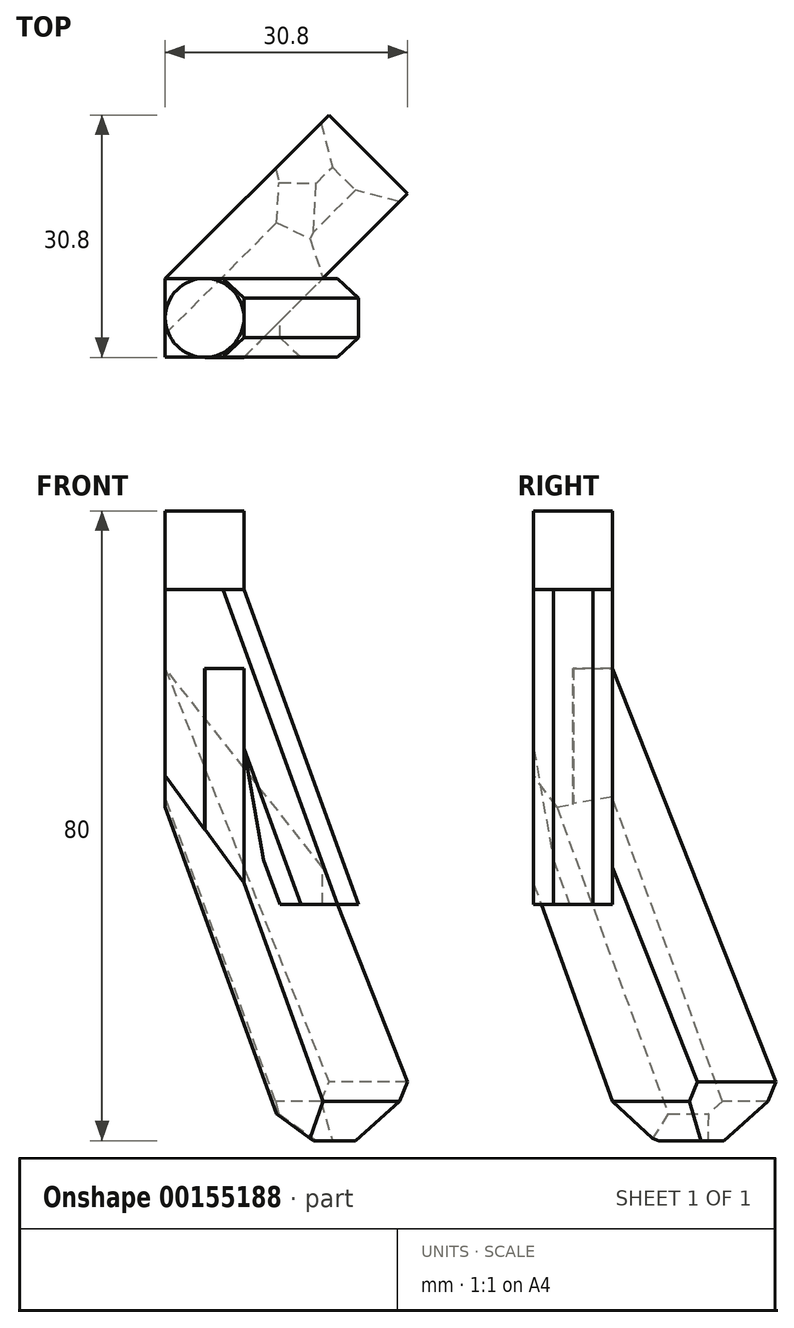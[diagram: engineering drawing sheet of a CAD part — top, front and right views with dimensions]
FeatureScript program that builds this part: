
annotation { "Feature Type Name" : "Feature", "Feature Type Description" : "" }
export const myFeature = defineFeature(function(context is Context, id is Id, definition is map)
    precondition{}
    {
        {
            var Q0;
            Q0=qCreatedBy(makeId("Top.planeOp"),FACE);
            var sketch = newSketch(context, id + "F0", { "sketchPlane" : qUnion([Q0])});
            skCircle(sketch, "E0", {"center": v(0, 0) * mm, "radius": 5 * mm});
            skSolve(sketch);
        }
        {
            var Q0;
            Q0=qSketchRegion(id+"F0",true);
            extrude(context, id + "F1", {"entities" : qUnion([Q0]), "oppositeDirection" : true, "depth" : 10 * mm});
        }
        {
            var Q0;
            Q0=makeQuery(id+"F1.opExtrude","CAP_FACE",FACE,{"disambiguationData":[OSD([sQuery(id+"F0.wireOp",EDGE,"E0")])],"isStart":false});
            var sketch = newSketch(context, id + "F2", { "sketchPlane" : qUnion([Q0])});
            skLineSegment(sketch, "E1.bottom", {"start": v(5, -5) * mm, "end": v(-5, -5) * mm});
            skLineSegment(sketch, "E1.top", {"start": v(5, 5) * mm, "end": v(-5, 5) * mm});
            skLineSegment(sketch, "E1.left", {"start": v(5, -5) * mm, "end": v(5, 5) * mm});
            skLineSegment(sketch, "E1.right", {"start": v(-5, -5) * mm, "end": v(-5, 5) * mm});
            skPoint(sketch, "E1.middle", {"position": v(0, 0) * mm});
            skSolve(sketch);
        }
        {
            var Q0;
            Q0=qSketchRegion(id+"F2",true);
            extrude(context, id + "F3", {"entities" : qUnion([Q0]), "operationType" : NewBodyOperationType.ADD, "depth" : 10 * mm});
        }
        {
            var Q0;
            Q0=makeQuery(id+"F3.opExtrude","CAP_FACE",FACE,{"disambiguationData":[OSD([sQuery(id+"F2.wireOp",EDGE,"E1.bottom"),sQuery(id+"F2.wireOp",EDGE,"E1.top"),sQuery(id+"F2.wireOp",EDGE,"E1.left"),sQuery(id+"F2.wireOp",EDGE,"E1.right")])],"isStart":false});
            var sketch = newSketch(context, id + "F4", { "sketchPlane" : qUnion([Q0])});
            skLineSegment(sketch, "E2", {"start": v(0, 5) * mm, "end": v(-5, 0) * mm});
            skLineSegment(sketch, "E3", {"start": v(-5, 0) * mm, "end": v(0, -5) * mm});
            skLineSegment(sketch, "E4", {"start": v(0, -5) * mm, "end": v(5, 0) * mm});
            skLineSegment(sketch, "E5", {"start": v(5, 0) * mm, "end": v(0, 5) * mm});
            skLineSegment(sketch, "E6", {"start": v(0, -5) * mm, "end": v(-2.5, -7.5) * mm});
            skLineSegment(sketch, "E7", {"start": v(-2.5, -7.5) * mm, "end": v(-5, -5) * mm});
            skLineSegment(sketch, "E8", {"start": v(-5, -5) * mm, "end": v(-7.5, -2.5) * mm});
            skLineSegment(sketch, "E9", {"start": v(-7.5, -2.5) * mm, "end": v(-5, 0) * mm});
            skLineSegment(sketch, "E10", {"start": v(0, 0) * mm, "end": v(5, -5) * mm});
            skLineSegment(sketch, "E11", {"start": v(5, -5) * mm, "end": v(-5, 5) * mm});
            skLineSegment(sketch, "E12.MirrorCS", {"start": v(5, 0) * mm, "end": v(7.5, 2.5) * mm});
            skLineSegment(sketch, "E13.MirrorCS", {"start": v(7.5, 2.5) * mm, "end": v(5, 5) * mm});
            skLineSegment(sketch, "E14.MirrorCS", {"start": v(5, 5) * mm, "end": v(2.5, 7.5) * mm});
            skLineSegment(sketch, "E15.MirrorCS", {"start": v(2.5, 7.5) * mm, "end": v(0, 5) * mm});
            skSolve(sketch);
        }
        {
            var Q0;
            {var subQ0=sQuery(id+"F4.wireOp",EDGE,"E6");Q0=makeQuery(id+"F4.imprint","IMPRINT",FACE,{"disambiguationData":[TD([[makeQuery(id+"F4.imprint","IMPRINT",EDGE,{"derivedFrom":subQ0}),-1.0]])]});}
            var Q1;
            {var subQ0=sQuery(id+"F4.wireOp",EDGE,"E8");Q1=makeQuery(id+"F4.imprint","IMPRINT",FACE,{"disambiguationData":[TD([[makeQuery(id+"F4.imprint","IMPRINT",EDGE,{"derivedFrom":subQ0}),-1.0]])]});}
            var Q2;
            {var subQ0=sQuery(id+"F4.wireOp",EDGE,"E12.MirrorCS");Q2=makeQuery(id+"F4.imprint","IMPRINT",FACE,{"disambiguationData":[TD([[makeQuery(id+"F4.imprint","IMPRINT",EDGE,{"derivedFrom":subQ0}),1.0]])]});}
            var Q3;
            {var subQ0=sQuery(id+"F4.wireOp",EDGE,"E14.MirrorCS");Q3=makeQuery(id+"F4.imprint","IMPRINT",FACE,{"disambiguationData":[TD([[makeQuery(id+"F4.imprint","IMPRINT",EDGE,{"derivedFrom":subQ0}),1.0]])]});}
            var Q4;
            {var subQ0=sQuery(id+"F4.wireOp",EDGE,"E3");Q4=makeQuery(id+"F4.imprint","IMPRINT",FACE,{"disambiguationData":[TD([[makeQuery(id+"F4.imprint","IMPRINT",EDGE,{"derivedFrom":subQ0}),-1.0]])]});}
            var Q5;
            {var subQ0=sQuery(id+"F4.wireOp",EDGE,"E5");Q5=makeQuery(id+"F4.imprint","IMPRINT",FACE,{"disambiguationData":[TD([[makeQuery(id+"F4.imprint","IMPRINT",EDGE,{"derivedFrom":subQ0}),-1.0]])]});}
            var Q6;
            {var subQ4=sQuery(id+"F4.wireOp",EDGE,"E3");Q6=makeQuery(id+"F4.imprint","IMPRINT",FACE,{"disambiguationData":[TD([[makeQuery(id+"F4.imprint","IMPRINT",EDGE,{"derivedFrom":subQ4}),1.0]])]});}
            var Q7;
            {var subQ4=sQuery(id+"F4.wireOp",EDGE,"E5");Q7=makeQuery(id+"F4.imprint","IMPRINT",FACE,{"disambiguationData":[TD([[makeQuery(id+"F4.imprint","IMPRINT",EDGE,{"derivedFrom":subQ4}),1.0]])]});}
            extrude(context, id + "F5", {"entities" : qUnion([Q0, Q1, Q2, Q3, Q4, Q5, Q6, Q7]), "operationType" : NewBodyOperationType.ADD, "depth" : 60 * mm});
        }
        {
            var Q0;
            Q0=makeQuery(id+"F5.opExtrude","SWEPT_FACE",FACE,{"disambiguationData":[OSD([sQuery(id+"F4.wireOp",EDGE,"E4"),sQuery(id+"F4.wireOp",EDGE,"E6"),sQuery(id+"F4.wireOp",EDGE,"E12.MirrorCS")])]});
            extrude(context, id + "F6", {"entities" : qUnion([Q0]), "operationType" : NewBodyOperationType.ADD, "depth" : 30 * mm});
        }
        {
            var Q0;
            {var subQ0=sQuery(id+"F2.wireOp",EDGE,"E1.top");var subQ1=sQuery(id+"F2.wireOp",EDGE,"E1.right");Q0=makeQuery(id+"F5.boolean.opBoolean","SPLIT",FACE,{"disambiguationData":[TD([makeQuery(id+"F3.opExtrude","SWEPT_FACE",FACE,{"disambiguationData":[OSD([subQ0])]})])],"derivedFrom":makeQuery(id+"F3.opExtrude","CAP_FACE",FACE,{"disambiguationData":[OSD([sQuery(id+"F2.wireOp",EDGE,"E1.bottom"),subQ0,sQuery(id+"F2.wireOp",EDGE,"E1.left"),subQ1])],"isStart":false})});}
            extrude(context, id + "F7", {"entities" : qUnion([Q0]), "operationType" : NewBodyOperationType.ADD, "depth" : 50 * mm});
        }
        {
            var Q0;
            {var subQ0=sQuery(id+"F4.wireOp",EDGE,"E7");Q0=makeQuery(id+"F6.boolean.opBoolean","MERGE",FACE,{"derivedFrom":[makeQuery(id+"F5.opExtrude","SWEPT_FACE",FACE,{"disambiguationData":[OSD([subQ0,sQuery(id+"F4.wireOp",EDGE,"E8")])]}),makeQuery(id+"F6.opExtrude","SWEPT_FACE",FACE,{"disambiguationData":[OSD([sQuery(id+"F4.wireOp",EDGE,"E6"),subQ0])]})]});}
            var sketch = newSketch(context, id + "F8", { "sketchPlane" : qUnion([Q0])});
            skLineSegment(sketch, "E16", {"start": v(0, -20) * mm, "end": v(-33.54, -80) * mm});
            skSolve(sketch);
        }
        {
            var Q0;
            Q0=makeQuery(id+"F8.imprint","IMPRINT",FACE,{"disambiguationData":[TD([[makeQuery(id+"F8.imprint","IMPRINT",EDGE,{"derivedFrom":sQuery(id+"F8.wireOp",EDGE,"E16")}),-1.0]])]});
            extrude(context, id + "F9", {"entities" : qUnion([Q0]), "operationType" : NewBodyOperationType.REMOVE, "oppositeDirection" : true, "depth" : 25 * mm});
        }
        {
            var Q0;
            Q0=makeQuery(id+"F9.boolean.opBoolean","COPY",FACE,{"derivedFrom":makeQuery(id+"F9.opExtrude","SWEPT_FACE",FACE,{"disambiguationData":[OSD([sQuery(id+"F4.wireOp",EDGE,"E6"),sQuery(id+"F4.wireOp",EDGE,"E7"),sQuery(id+"F4.wireOp",EDGE,"E8")])]})});
            extrude(context, id + "F10", {"entities" : qUnion([Q0]), "operationType" : NewBodyOperationType.ADD, "depth" : 25 * mm});
        }
        {
            var Q0;
            Q0=makeQuery(id+"F5.opExtrude","SWEPT_EDGE",EDGE,{"disambiguationData":[OSD([sQuery(id+"F4.wireOp",EDGE,"E8"),sQuery(id+"F4.wireOp",EDGE,"E9")])]});
            var Q1;
            Q1=makeQuery(id+"F5.opExtrude","SWEPT_EDGE",EDGE,{"disambiguationData":[OSD([sQuery(id+"F4.wireOp",EDGE,"E14.MirrorCS"),sQuery(id+"F4.wireOp",EDGE,"E15.MirrorCS")])]});
            chamfer(context, id + "F11", {"entities" : qUnion([Q0, Q1]), "width" : 3.5 * mm, "tangentPropagation" : true});
        }
        {
            var Q0;
            {var subQ0=sQuery(id+"F4.wireOp",EDGE,"E13.MirrorCS");Q0=makeQuery(id+"F6.boolean.opBoolean","MERGE",FACE,{"derivedFrom":[makeQuery(id+"F5.opExtrude","SWEPT_FACE",FACE,{"disambiguationData":[OSD([subQ0,sQuery(id+"F4.wireOp",EDGE,"E14.MirrorCS")])]}),makeQuery(id+"F6.opExtrude","SWEPT_FACE",FACE,{"disambiguationData":[OSD([sQuery(id+"F4.wireOp",EDGE,"E12.MirrorCS"),subQ0])]})]});}
            var sketch = newSketch(context, id + "F12", { "sketchPlane" : qUnion([Q0])});
            skLineSegment(sketch, "E17", {"start": v(-0.04, -80) * mm, "end": v(-14.04, -20) * mm});
            skLineSegment(sketch, "E18", {"start": v(-14.04, -20) * mm, "end": v(0, -20) * mm});
            skLineSegment(sketch, "E19.bottom", {"start": v(-14.04, -20) * mm, "end": v(-0.04, -20) * mm});
            skLineSegment(sketch, "E19.top", {"start": v(-14.04, -80) * mm, "end": v(-0.04, -80) * mm});
            skLineSegment(sketch, "E19.left", {"start": v(-14.04, -20) * mm, "end": v(-14.04, -80) * mm});
            skLineSegment(sketch, "E19.right", {"start": v(-0.04, -20) * mm, "end": v(-0.04, -80) * mm});
            skLineSegment(sketch, "E20", {"start": v(-14.04, -20) * mm, "end": v(16.75, -80) * mm});
            skSolve(sketch);
        }
        {
            var Q0;
            Q0=makeQuery(id+"F12.imprint","IMPRINT",FACE,{"disambiguationData":[TD([[makeQuery(id+"F12.imprint","IMPRINT",EDGE,{"derivedFrom":sQuery(id+"F12.wireOp",EDGE,"E17")}),1.0]])]});
            var Q1;
            {var subQ0=sQuery(id+"F12.wireOp",EDGE,"E19.right");var subQ5=sQuery(id+"F12.wireOp",EDGE,"E20");var subQ6=makeQuery(id+"F12.imprint","INTERSECT",VERTEX,{"derivedFrom":[subQ0,subQ5]});Q1=makeQuery(id+"F12.imprint","IMPRINT",FACE,{"disambiguationData":[TD([[makeQuery(id+"F12.imprint","IMPRINT",EDGE,{"disambiguationData":[TD([[subQ6,-1.0]])],"derivedFrom":subQ5}),-1.0]])]});}
            var Q2;
            {var subQ0=sQuery(id+"F12.wireOp",EDGE,"E17");Q2=makeQuery(id+"F12.imprint","IMPRINT",FACE,{"disambiguationData":[TD([[makeQuery(id+"F12.imprint","IMPRINT",EDGE,{"derivedFrom":subQ0}),-1.0]])]});}
            extrude(context, id + "F13", {"entities" : qUnion([Q0, Q1, Q2]), "operationType" : NewBodyOperationType.REMOVE, "oppositeDirection" : true, "depth" : 25 * mm});
        }
        {
            var Q0;
            {var subQ0=sQuery(id+"F4.wireOp",EDGE,"E7");Q0=makeQuery(id+"F13.boolean.opBoolean","INTERSECT",EDGE,{"derivedFrom":[makeQuery(id+"F6.boolean.opBoolean","MERGE",FACE,{"derivedFrom":[makeQuery(id+"F5.opExtrude","SWEPT_FACE",FACE,{"disambiguationData":[OSD([subQ0,sQuery(id+"F4.wireOp",EDGE,"E8")])]}),makeQuery(id+"F6.opExtrude","SWEPT_FACE",FACE,{"disambiguationData":[OSD([sQuery(id+"F4.wireOp",EDGE,"E6"),subQ0])]})]}),makeQuery(id+"F13.opExtrude","SWEPT_FACE",FACE,{"disambiguationData":[OSD([sQuery(id+"F12.wireOp",EDGE,"E20")])]})]});}
            var Q1;
            Q1=makeQuery(id+"F13.boolean.opBoolean","COPY",EDGE,{"derivedFrom":makeQuery(id+"F13.opExtrude","CAP_EDGE",EDGE,{"disambiguationData":[OSD([sQuery(id+"F12.wireOp",EDGE,"E20")])],"isStart":true})});
            chamfer(context, id + "F14", {"entities" : qUnion([Q0, Q1]), "width" : 5 * mm, "tangentPropagation" : true});
        }
        {
            var Q0;
            {var subQ0=sQuery(id+"F4.wireOp",EDGE,"E13.MirrorCS");var subQ1=sQuery(id+"F4.wireOp",EDGE,"E12.MirrorCS");Q0=makeQuery(id+"F6.boolean.opBoolean","MERGE",EDGE,{"derivedFrom":[makeQuery(id+"F5.opExtrude","CAP_EDGE",EDGE,{"disambiguationData":[OSD([subQ0,sQuery(id+"F4.wireOp",EDGE,"E14.MirrorCS")])],"isStart":false}),makeQuery(id+"F6.opExtrude","SWEPT_EDGE",EDGE,{"disambiguationData":[OSD([subQ1,subQ0]),TDD([makeQuery(id+"F5.opExtrude","CAP_VERTEX",VERTEX,{"disambiguationData":[OSD([subQ1,subQ0])],"isStart":false})])]})]});}
            var Q1;
            {var subQ0=sQuery(id+"F8.wireOp",EDGE,"E16");var subQ1=sQuery(id+"F4.wireOp",EDGE,"E7");var subQ2=sQuery(id+"F4.wireOp",EDGE,"E6");var subQ3=sQuery(id+"F4.wireOp",EDGE,"E8");var subQ4=sQuery(id+"F4.wireOp",EDGE,"E12.MirrorCS");var subQ5=sQuery(id+"F4.wireOp",EDGE,"E4");Q1=makeQuery(id+"F9.boolean.opBoolean","MERGE",EDGE,{"derivedFrom":[makeQuery(id+"F6.opExtrude","CAP_EDGE",EDGE,{"disambiguationData":[OSD([subQ5,subQ2,subQ4]),TDD([makeQuery(id+"F5.opExtrude","CAP_EDGE",EDGE,{"disambiguationData":[OSD([subQ5,subQ2,subQ4])],"isStart":false})])],"isStart":false}),makeQuery(id+"F9.opExtrude","SWEPT_EDGE",EDGE,{"disambiguationData":[OSD([subQ2,subQ1,subQ3,subQ0]),TDD([makeQuery(id+"F8.imprint","INTERSECT",VERTEX,{"derivedFrom":[makeQuery(id+"F6.opExtrude","CAP_EDGE",EDGE,{"disambiguationData":[OSD([subQ2,subQ1])],"isStart":false}),makeQuery(id+"F6.boolean.opBoolean","MERGE",EDGE,{"derivedFrom":[makeQuery(id+"F5.opExtrude","CAP_EDGE",EDGE,{"disambiguationData":[OSD([subQ1,subQ3])],"isStart":false}),makeQuery(id+"F6.opExtrude","SWEPT_EDGE",EDGE,{"disambiguationData":[OSD([subQ2,subQ1]),TDD([makeQuery(id+"F5.opExtrude","CAP_VERTEX",VERTEX,{"disambiguationData":[OSD([subQ2,subQ1])],"isStart":false})])]})]}),subQ0]})])]})]});}
            var Q2;
            {var subQ0=sQuery(id+"F4.wireOp",EDGE,"E7");var subQ1=sQuery(id+"F4.wireOp",EDGE,"E6");Q2=makeQuery(id+"F6.boolean.opBoolean","MERGE",EDGE,{"derivedFrom":[makeQuery(id+"F5.opExtrude","CAP_EDGE",EDGE,{"disambiguationData":[OSD([subQ0,sQuery(id+"F4.wireOp",EDGE,"E8")])],"isStart":false}),makeQuery(id+"F6.opExtrude","SWEPT_EDGE",EDGE,{"disambiguationData":[OSD([subQ1,subQ0]),TDD([makeQuery(id+"F5.opExtrude","CAP_VERTEX",VERTEX,{"disambiguationData":[OSD([subQ1,subQ0])],"isStart":false})])]})]});}
            var Q3;
            {var subQ0=sQuery(id+"F4.wireOp",EDGE,"E12.MirrorCS");var subQ1=sQuery(id+"F4.wireOp",EDGE,"E6");var subQ2=sQuery(id+"F4.wireOp",EDGE,"E4");var subQ3=sQuery(id+"F4.wireOp",EDGE,"E8");var subQ4=sQuery(id+"F4.wireOp",EDGE,"E7");Q3=makeQuery(id+"F14.opChamfer","BLEND_EDGE",EDGE,{"blendedFrom":[makeQuery(id+"F13.boolean.opBoolean","INTERSECT",EDGE,{"derivedFrom":[makeQuery(id+"F6.boolean.opBoolean","MERGE",FACE,{"derivedFrom":[makeQuery(id+"F5.opExtrude","SWEPT_FACE",FACE,{"disambiguationData":[OSD([subQ4,subQ3])]}),makeQuery(id+"F6.opExtrude","SWEPT_FACE",FACE,{"disambiguationData":[OSD([subQ1,subQ4])]})]}),makeQuery(id+"F13.opExtrude","SWEPT_FACE",FACE,{"disambiguationData":[OSD([sQuery(id+"F12.wireOp",EDGE,"E20")])]})]}),makeQuery(id+"F6.boolean.opBoolean","MERGE",FACE,{"derivedFrom":[makeQuery(id+"F5.opExtrude","CAP_FACE",FACE,{"disambiguationData":[OSD([sQuery(id+"F4.wireOp",EDGE,"E2"),subQ2,subQ1,subQ4,subQ3,sQuery(id+"F4.wireOp",EDGE,"E9"),subQ0,sQuery(id+"F4.wireOp",EDGE,"E13.MirrorCS"),sQuery(id+"F4.wireOp",EDGE,"E14.MirrorCS"),sQuery(id+"F4.wireOp",EDGE,"E15.MirrorCS")])],"isStart":false}),makeQuery(id+"F6.opExtrude","SWEPT_FACE",FACE,{"disambiguationData":[OSD([subQ2,subQ1,subQ0]),TDD([makeQuery(id+"F5.opExtrude","CAP_EDGE",EDGE,{"disambiguationData":[OSD([subQ2,subQ1,subQ0])],"isStart":false})])]})]})],"blendedInto":[makeQuery(id+"F6.boolean.opBoolean","MERGE",FACE,{"derivedFrom":[makeQuery(id+"F5.opExtrude","CAP_FACE",FACE,{"disambiguationData":[OSD([sQuery(id+"F4.wireOp",EDGE,"E2"),subQ2,subQ1,subQ4,subQ3,sQuery(id+"F4.wireOp",EDGE,"E9"),subQ0,sQuery(id+"F4.wireOp",EDGE,"E13.MirrorCS"),sQuery(id+"F4.wireOp",EDGE,"E14.MirrorCS"),sQuery(id+"F4.wireOp",EDGE,"E15.MirrorCS")])],"isStart":false}),makeQuery(id+"F6.opExtrude","SWEPT_FACE",FACE,{"disambiguationData":[OSD([subQ2,subQ1,subQ0]),TDD([makeQuery(id+"F5.opExtrude","CAP_EDGE",EDGE,{"disambiguationData":[OSD([subQ2,subQ1,subQ0])],"isStart":false})])]})]})]});}
            var Q4;
            Q4=makeQuery(id+"F13.boolean.opBoolean","COPY",EDGE,{"derivedFrom":makeQuery(id+"F13.opExtrude","SWEPT_EDGE",EDGE,{"disambiguationData":[OSD([sQuery(id+"F4.wireOp",EDGE,"E12.MirrorCS"),sQuery(id+"F4.wireOp",EDGE,"E13.MirrorCS"),sQuery(id+"F4.wireOp",EDGE,"E14.MirrorCS"),sQuery(id+"F12.wireOp",EDGE,"E20")])]})});
            var Q5;
            {var subQ0=sQuery(id+"F4.wireOp",EDGE,"E12.MirrorCS");var subQ1=sQuery(id+"F4.wireOp",EDGE,"E6");var subQ2=sQuery(id+"F4.wireOp",EDGE,"E4");Q5=makeQuery(id+"F14.opChamfer","BLEND_EDGE",EDGE,{"blendedFrom":[makeQuery(id+"F13.boolean.opBoolean","COPY",EDGE,{"derivedFrom":makeQuery(id+"F13.opExtrude","CAP_EDGE",EDGE,{"disambiguationData":[OSD([sQuery(id+"F12.wireOp",EDGE,"E20")])],"isStart":true})}),makeQuery(id+"F6.boolean.opBoolean","MERGE",FACE,{"derivedFrom":[makeQuery(id+"F5.opExtrude","CAP_FACE",FACE,{"disambiguationData":[OSD([sQuery(id+"F4.wireOp",EDGE,"E2"),subQ2,subQ1,sQuery(id+"F4.wireOp",EDGE,"E7"),sQuery(id+"F4.wireOp",EDGE,"E8"),sQuery(id+"F4.wireOp",EDGE,"E9"),subQ0,sQuery(id+"F4.wireOp",EDGE,"E13.MirrorCS"),sQuery(id+"F4.wireOp",EDGE,"E14.MirrorCS"),sQuery(id+"F4.wireOp",EDGE,"E15.MirrorCS")])],"isStart":false}),makeQuery(id+"F6.opExtrude","SWEPT_FACE",FACE,{"disambiguationData":[OSD([subQ2,subQ1,subQ0]),TDD([makeQuery(id+"F5.opExtrude","CAP_EDGE",EDGE,{"disambiguationData":[OSD([subQ2,subQ1,subQ0])],"isStart":false})])]})]})],"blendedInto":[makeQuery(id+"F6.boolean.opBoolean","MERGE",FACE,{"derivedFrom":[makeQuery(id+"F5.opExtrude","CAP_FACE",FACE,{"disambiguationData":[OSD([sQuery(id+"F4.wireOp",EDGE,"E2"),subQ2,subQ1,sQuery(id+"F4.wireOp",EDGE,"E7"),sQuery(id+"F4.wireOp",EDGE,"E8"),sQuery(id+"F4.wireOp",EDGE,"E9"),subQ0,sQuery(id+"F4.wireOp",EDGE,"E13.MirrorCS"),sQuery(id+"F4.wireOp",EDGE,"E14.MirrorCS"),sQuery(id+"F4.wireOp",EDGE,"E15.MirrorCS")])],"isStart":false}),makeQuery(id+"F6.opExtrude","SWEPT_FACE",FACE,{"disambiguationData":[OSD([subQ2,subQ1,subQ0]),TDD([makeQuery(id+"F5.opExtrude","CAP_EDGE",EDGE,{"disambiguationData":[OSD([subQ2,subQ1,subQ0])],"isStart":false})])]})]})]});}
            chamfer(context, id + "F15", {"entities" : qUnion([Q0, Q1, Q2, Q3, Q4, Q5]), "width" : 5 * mm, "tangentPropagation" : true});
        }
        {
            var Q0;
            Q0=qCreatedBy(makeId("Front.planeOp"),FACE);
            var sketch = newSketch(context, id + "F16", { "sketchPlane" : qUnion([Q0])});
            skLineSegment(sketch, "E21.bottom", {"start": v(0, 0) * mm, "end": v(30, 0) * mm});
            skLineSegment(sketch, "E21.top", {"start": v(0, -50) * mm, "end": v(30, -50) * mm});
            skLineSegment(sketch, "E21.left", {"start": v(0, 0) * mm, "end": v(0, -50) * mm});
            skLineSegment(sketch, "E21.right", {"start": v(30, 0) * mm, "end": v(30, -50) * mm});
            skLineSegment(sketch, "E22", {"start": v(0, 0) * mm, "end": v(-5, 0) * mm});
            skLineSegment(sketch, "E23.bottom", {"start": v(-5, 0) * mm, "end": v(0, 0) * mm});
            skLineSegment(sketch, "E23.top", {"start": v(-5, -10) * mm, "end": v(0, -10) * mm});
            skLineSegment(sketch, "E23.left", {"start": v(-5, 0) * mm, "end": v(-5, -10) * mm});
            skLineSegment(sketch, "E23.right", {"start": v(0, 0) * mm, "end": v(0, -10) * mm});
            skLineSegment(sketch, "E24.bottom", {"start": v(0, -10) * mm, "end": v(5, -10) * mm});
            skLineSegment(sketch, "E24.top", {"start": v(0, 0) * mm, "end": v(5, 0) * mm});
            skLineSegment(sketch, "E24.left", {"start": v(0, -10) * mm, "end": v(0, 0) * mm});
            skLineSegment(sketch, "E24.right", {"start": v(5, -10) * mm, "end": v(5, 0) * mm});
            skLineSegment(sketch, "E25", {"start": v(-5, -10) * mm, "end": v(9.56, -50) * mm});
            skLineSegment(sketch, "E26", {"start": v(5, -10) * mm, "end": v(19.56, -50) * mm});
            skSolve(sketch);
        }
        {
            var Q0;
            {var subQ0=sQuery(id+"F16.wireOp",EDGE,"E23.top");Q0=makeQuery(id+"F16.imprint","IMPRINT",FACE,{"disambiguationData":[TD([[makeQuery(id+"F16.imprint","IMPRINT",EDGE,{"derivedFrom":subQ0}),-1.0]])]});}
            var Q1;
            {var subQ0=sQuery(id+"F16.wireOp",EDGE,"E24.bottom");Q1=makeQuery(id+"F16.imprint","IMPRINT",FACE,{"disambiguationData":[TD([[makeQuery(id+"F16.imprint","IMPRINT",EDGE,{"derivedFrom":subQ0}),-1.0]])]});}
            extrude(context, id + "F17", {"entities" : qUnion([Q0, Q1]), "endBound" : BoundingType.SYMMETRIC, "depth" : 10 * mm});
        }
        {
            var Q0;
            Q0=makeQuery(id+"F0.imprint","IMPRINT",FACE,{"disambiguationData":[TD([[makeQuery(id+"F0.imprint","IMPRINT",EDGE,{"derivedFrom":sQuery(id+"F0.wireOp",EDGE,"E0")}),1.0]])]});
            var Q1;
            Q1=makeQuery(id+"F17.opExtrude","SWEPT_FACE",FACE,{"disambiguationData":[OSD([sQuery(id+"F16.wireOp",EDGE,"E23.top"),sQuery(id+"F16.wireOp",EDGE,"E24.bottom")])]});
            extrude(context, id + "F18", {"entities" : qUnion([Q0]), "operationType" : NewBodyOperationType.ADD, "endBound" : BoundingType.UP_TO_SURFACE, "oppositeDirection" : true, "endBoundEntityFace" : qUnion([Q1]), "depth" : 25 * mm});
        }
        {
            var Q0;
            Q0=makeQuery(id+"F17.opExtrude","CAP_EDGE",EDGE,{"disambiguationData":[OSD([sQuery(id+"F16.wireOp",EDGE,"E26")])],"isStart":false});
            var Q1;
            Q1=makeQuery(id+"F17.opExtrude","CAP_EDGE",EDGE,{"disambiguationData":[OSD([sQuery(id+"F16.wireOp",EDGE,"E26")])],"isStart":true});
            var Q2;
            Q2=makeQuery(id+"F17.opExtrude","CAP_EDGE",EDGE,{"disambiguationData":[OSD([sQuery(id+"F16.wireOp",EDGE,"E25")])],"isStart":false});
            var Q3;
            Q3=makeQuery(id+"F17.opExtrude","CAP_EDGE",EDGE,{"disambiguationData":[OSD([sQuery(id+"F16.wireOp",EDGE,"E25")])],"isStart":true});
            chamfer(context, id + "F19", {"entities" : qUnion([Q0, Q1, Q2, Q3]), "width" : 2.5 * mm, "tangentPropagation" : true});
        }
    });
